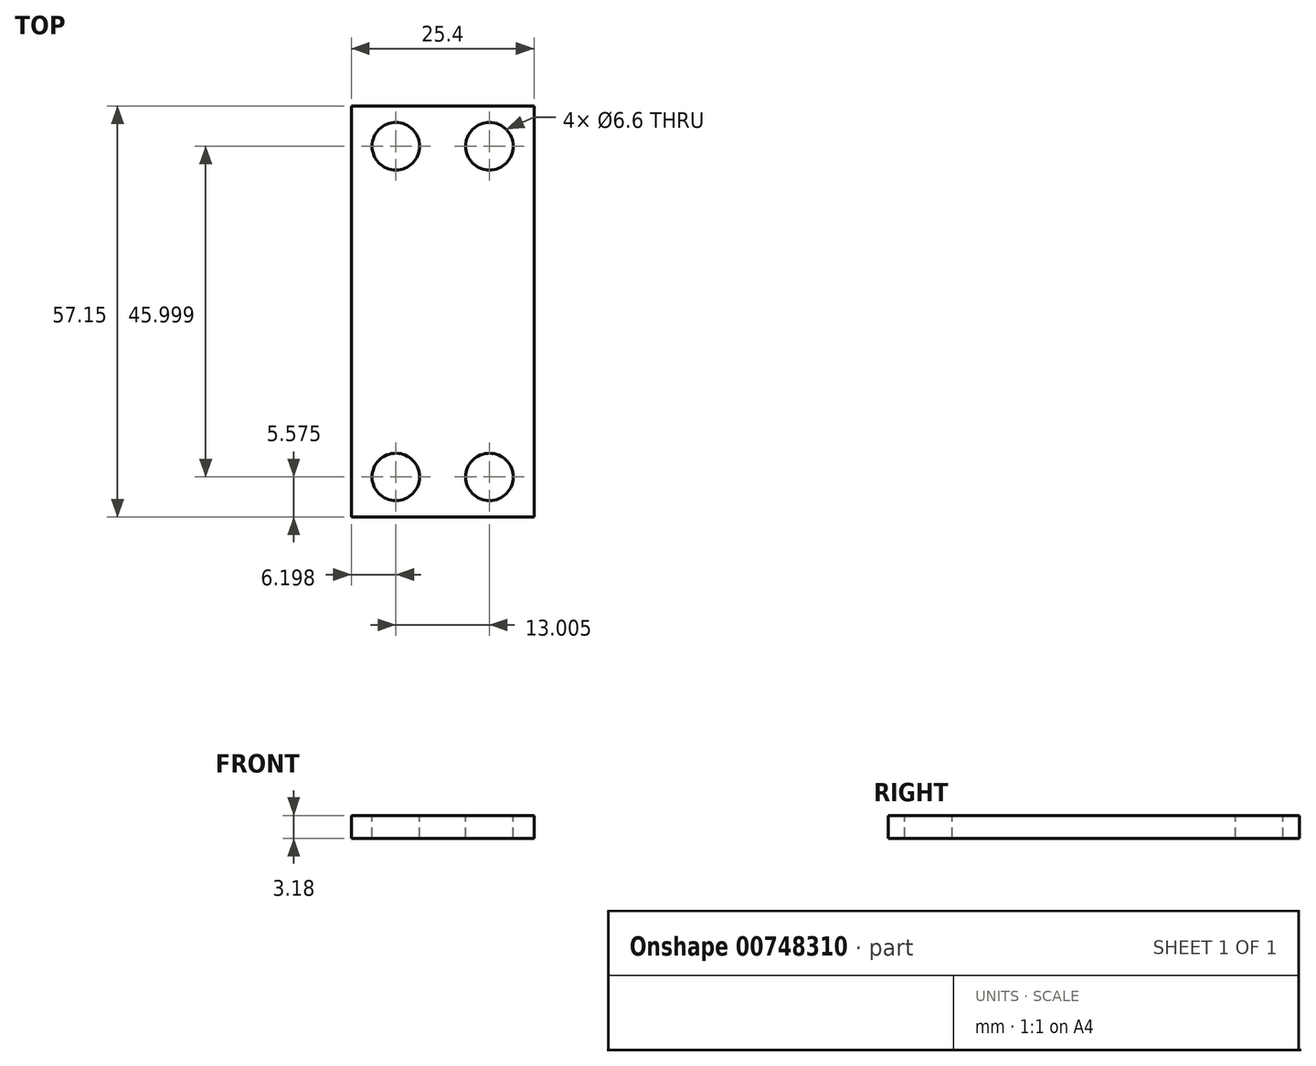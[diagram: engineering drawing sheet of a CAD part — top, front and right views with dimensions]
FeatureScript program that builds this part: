
annotation { "Feature Type Name" : "Feature", "Feature Type Description" : "" }
export const myFeature = defineFeature(function(context is Context, id is Id, definition is map)
    precondition{}
    {
        {
            var Q0;
            Q0=qCreatedBy(makeId("Front.planeOp"),FACE);
            var sketch = newSketch(context, id + "F0", { "sketchPlane" : qUnion([Q0])});
            skLineSegment(sketch, "E0.bottom", {"start": v(12.7, -1.59) * mm, "end": v(-12.7, -1.59) * mm});
            skLineSegment(sketch, "E0.top", {"start": v(12.7, 1.59) * mm, "end": v(-12.7, 1.59) * mm});
            skLineSegment(sketch, "E0.left", {"start": v(12.7, -1.59) * mm, "end": v(12.7, 1.59) * mm});
            skLineSegment(sketch, "E0.right", {"start": v(-12.7, -1.59) * mm, "end": v(-12.7, 1.59) * mm});
            skPoint(sketch, "E0.middle", {"position": v(0, 0) * mm});
            skSolve(sketch);
        }
        {
            var Q0;
            Q0=qSketchRegion(id+"F0",true);
            extrude(context, id + "F1", {"entities" : qUnion([Q0]), "depth" : 57.15 * mm, "offsetDistance" : 25.4 * mm});
        }
        {
            var Q0;
            Q0=makeQuery(id+"F1.opExtrude","SWEPT_FACE",FACE,{"disambiguationData":[OSD([sQuery(id+"F0.wireOp",EDGE,"E0.top")])]});
            var sketch = newSketch(context, id + "F2", { "sketchPlane" : qUnion([Q0])});
            skLineSegment(sketch, "E1", {"start": v(0, -57.15) * mm, "end": v(0, 0) * mm, "construction": true});
            skLineSegment(sketch, "E2", {"start": v(-12.7, -41.28) * mm, "end": v(12.7, -41.28) * mm, "construction": true});
            skLineSegment(sketch, "E3", {"start": v(-12.7, -15.88) * mm, "end": v(12.7, -15.88) * mm, "construction": true});
            skLineSegment(sketch, "E4", {"start": v(-12.7, -28.58) * mm, "end": v(12.7, -28.58) * mm, "construction": true});
            skLineSegment(sketch, "E5.bottom", {"start": v(6.5, -5.58) * mm, "end": v(-6.5, -5.58) * mm, "construction": true});
            skLineSegment(sketch, "E5.top", {"start": v(6.5, -51.57) * mm, "end": v(-6.5, -51.57) * mm, "construction": true});
            skLineSegment(sketch, "E5.left", {"start": v(6.5, -5.58) * mm, "end": v(6.5, -51.57) * mm, "construction": true});
            skLineSegment(sketch, "E5.right", {"start": v(-6.5, -5.58) * mm, "end": v(-6.5, -51.57) * mm, "construction": true});
            skPoint(sketch, "E5.middle", {"position": v(0, -28.58) * mm});
            skCircle(sketch, "E6", {"center": v(-6.5, -5.58) * mm, "radius": 3.3 * mm});
            skCircle(sketch, "E7", {"center": v(6.5, -5.58) * mm, "radius": 3.3 * mm});
            skCircle(sketch, "E8", {"center": v(6.5, -51.57) * mm, "radius": 3.3 * mm});
            skCircle(sketch, "E9", {"center": v(-6.5, -51.57) * mm, "radius": 3.3 * mm});
            skSolve(sketch);
        }
        {
            var Q0;
            Q0=qSketchRegion(id+"F2",true);
            extrude(context, id + "F3", {"entities" : qUnion([Q0]), "operationType" : NewBodyOperationType.REMOVE, "endBound" : BoundingType.THROUGH_ALL, "oppositeDirection" : true, "depth" : 25.4 * mm, "offsetDistance" : 25.4 * mm});
        }
    });
